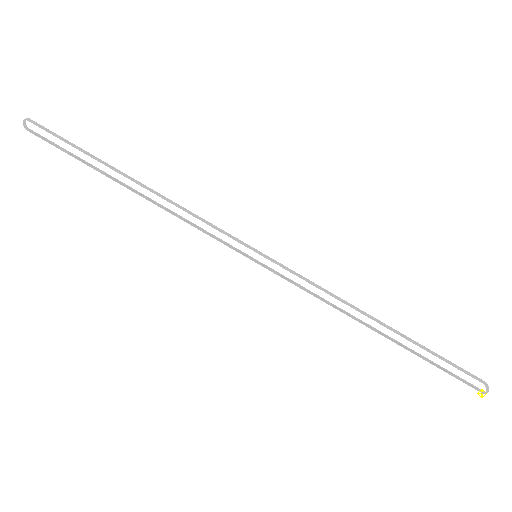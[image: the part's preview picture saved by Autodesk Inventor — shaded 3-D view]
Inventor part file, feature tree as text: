
AUTODESK INVENTOR PART (.ipt)
format: ipt  version: 2025.1 (Build 291241000, 241)  size: 7,425,536 bytes
history: native  units: mm
features: other x361, sketch x3, pattern_linear x2, extrude x2
ambient origin geometry x8: Origin, YZ Plane, XZ Plane, XY Plane, X Axis, Y Axis, Z Axis, Center Point
bodies: Body1 (feature_tree)
feature tree (368):
  other  "Bryła1"
  sketch  "Szkic1"
  other  "Punkt konstrukcyjny1"
  pattern_linear  "Szyk prostokątny1"  Spacing1=27.95mm  [1 undecoded]
  extrude  "Wyciągnięcie proste1"  Depth=1439.872mm
  pattern_linear  "Szyk prostokątny2"  Count1=360 Spacing1=10.0mm
  extrude  "Wyciągnięcie proste2"  Depth=1.0mm
  other  "Punkt konstrukcyjny2"
  other  "Punkt konstrukcyjny3"
  other  "Punkt konstrukcyjny4"
  other  "Punkt konstrukcyjny5"
  other  "Punkt konstrukcyjny6"
  other  "Punkt konstrukcyjny7"
  other  "Punkt konstrukcyjny8"
  other  "Punkt konstrukcyjny9"
  other  "Punkt konstrukcyjny10"
  other  "Punkt konstrukcyjny11"
  other  "Punkt konstrukcyjny12"
  other  "Punkt konstrukcyjny13"
  other  "Punkt konstrukcyjny14"
  other  "Punkt konstrukcyjny15"
  other  "Punkt konstrukcyjny16"
  other  "Punkt konstrukcyjny17"
  other  "Punkt konstrukcyjny18"
  other  "Punkt konstrukcyjny19"
  other  "Punkt konstrukcyjny20"
  other  "Punkt konstrukcyjny21"
  other  "Punkt konstrukcyjny22"
  other  "Punkt konstrukcyjny23"
  other  "Punkt konstrukcyjny24"
  other  "Punkt konstrukcyjny25"
  other  "Punkt konstrukcyjny26"
  other  "Punkt konstrukcyjny27"
  other  "Punkt konstrukcyjny28"
  other  "Punkt konstrukcyjny29"
  other  "Punkt konstrukcyjny30"
  other  "Punkt konstrukcyjny31"
  other  "Punkt konstrukcyjny32"
  other  "Punkt konstrukcyjny33"
  other  "Punkt konstrukcyjny34"
  other  "Punkt konstrukcyjny35"
  other  "Punkt konstrukcyjny36"
  other  "Punkt konstrukcyjny37"
  other  "Punkt konstrukcyjny38"
  other  "Punkt konstrukcyjny39"
  other  "Punkt konstrukcyjny40"
  other  "Punkt konstrukcyjny41"
  other  "Punkt konstrukcyjny42"
  other  "Punkt konstrukcyjny43"
  other  "Punkt konstrukcyjny44"
  other  "Punkt konstrukcyjny45"
  other  "Punkt konstrukcyjny46"
  other  "Punkt konstrukcyjny47"
  other  "Punkt konstrukcyjny48"
  other  "Punkt konstrukcyjny49"
  other  "Punkt konstrukcyjny50"
  other  "Punkt konstrukcyjny51"
  other  "Punkt konstrukcyjny52"
  other  "Punkt konstrukcyjny53"
  other  "Punkt konstrukcyjny54"
  other  "Punkt konstrukcyjny55"
  other  "Punkt konstrukcyjny56"
  other  "Punkt konstrukcyjny57"
  other  "Punkt konstrukcyjny58"
  other  "Punkt konstrukcyjny59"
  other  "Punkt konstrukcyjny60"
  other  "Punkt konstrukcyjny61"
  other  "Punkt konstrukcyjny62"
  other  "Punkt konstrukcyjny63"
  other  "Punkt konstrukcyjny64"
  other  "Punkt konstrukcyjny65"
  other  "Punkt konstrukcyjny66"
  other  "Punkt konstrukcyjny67"
  other  "Punkt konstrukcyjny68"
  other  "Punkt konstrukcyjny69"
  other  "Punkt konstrukcyjny70"
  other  "Punkt konstrukcyjny71"
  other  "Punkt konstrukcyjny72"
  other  "Punkt konstrukcyjny73"
  other  "Punkt konstrukcyjny74"
  other  "Punkt konstrukcyjny75"
  other  "Punkt konstrukcyjny76"
  other  "Punkt konstrukcyjny77"
  other  "Punkt konstrukcyjny78"
  other  "Punkt konstrukcyjny79"
  other  "Punkt konstrukcyjny80"
  other  "Punkt konstrukcyjny81"
  other  "Punkt konstrukcyjny82"
  other  "Punkt konstrukcyjny83"
  other  "Punkt konstrukcyjny84"
  other  "Punkt konstrukcyjny85"
  other  "Punkt konstrukcyjny86"
  other  "Punkt konstrukcyjny87"
  other  "Punkt konstrukcyjny88"
  other  "Punkt konstrukcyjny89"
  other  "Punkt konstrukcyjny90"
  other  "Punkt konstrukcyjny91"
  other  "Punkt konstrukcyjny92"
  other  "Punkt konstrukcyjny93"
  other  "Punkt konstrukcyjny94"
  other  "Punkt konstrukcyjny95"
  other  "Punkt konstrukcyjny96"
  other  "Punkt konstrukcyjny97"
  other  "Punkt konstrukcyjny98"
  other  "Punkt konstrukcyjny99"
  other  "Punkt konstrukcyjny100"
  other  "Punkt konstrukcyjny101"
  other  "Punkt konstrukcyjny102"
  other  "Punkt konstrukcyjny103"
  other  "Punkt konstrukcyjny104"
  other  "Punkt konstrukcyjny105"
  other  "Punkt konstrukcyjny106"
  other  "Punkt konstrukcyjny107"
  other  "Punkt konstrukcyjny108"
  other  "Punkt konstrukcyjny109"
  other  "Punkt konstrukcyjny110"
  other  "Punkt konstrukcyjny111"
  other  "Punkt konstrukcyjny112"
  other  "Punkt konstrukcyjny113"
  other  "Punkt konstrukcyjny114"
  other  "Punkt konstrukcyjny115"
  other  "Punkt konstrukcyjny116"
  other  "Punkt konstrukcyjny117"
  other  "Punkt konstrukcyjny118"
  other  "Punkt konstrukcyjny119"
  other  "Punkt konstrukcyjny120"
  other  "Punkt konstrukcyjny121"
  other  "Punkt konstrukcyjny122"
  other  "Punkt konstrukcyjny123"
  other  "Punkt konstrukcyjny124"
  other  "Punkt konstrukcyjny125"
  other  "Punkt konstrukcyjny126"
  other  "Punkt konstrukcyjny127"
  other  "Punkt konstrukcyjny128"
  other  "Punkt konstrukcyjny129"
  other  "Punkt konstrukcyjny130"
  other  "Punkt konstrukcyjny131"
  other  "Punkt konstrukcyjny132"
  other  "Punkt konstrukcyjny133"
  other  "Punkt konstrukcyjny134"
  other  "Punkt konstrukcyjny135"
  other  "Punkt konstrukcyjny136"
  other  "Punkt konstrukcyjny137"
  other  "Punkt konstrukcyjny138"
  other  "Punkt konstrukcyjny139"
  other  "Punkt konstrukcyjny140"
  other  "Punkt konstrukcyjny141"
  other  "Punkt konstrukcyjny142"
  other  "Punkt konstrukcyjny143"
  other  "Punkt konstrukcyjny144"
  other  "Punkt konstrukcyjny145"
  other  "Punkt konstrukcyjny146"
  other  "Punkt konstrukcyjny147"
  other  "Punkt konstrukcyjny148"
  other  "Punkt konstrukcyjny149"
  other  "Punkt konstrukcyjny150"
  other  "Punkt konstrukcyjny151"
  other  "Punkt konstrukcyjny152"
  other  "Punkt konstrukcyjny153"
  other  "Punkt konstrukcyjny154"
  other  "Punkt konstrukcyjny155"
  other  "Punkt konstrukcyjny156"
  other  "Punkt konstrukcyjny157"
  other  "Punkt konstrukcyjny158"
  other  "Punkt konstrukcyjny159"
  other  "Punkt konstrukcyjny160"
  other  "Punkt konstrukcyjny161"
  other  "Punkt konstrukcyjny162"
  other  "Punkt konstrukcyjny163"
  other  "Punkt konstrukcyjny164"
  other  "Punkt konstrukcyjny165"
  other  "Punkt konstrukcyjny166"
  other  "Punkt konstrukcyjny167"
  other  "Punkt konstrukcyjny168"
  other  "Punkt konstrukcyjny169"
  other  "Punkt konstrukcyjny170"
  other  "Punkt konstrukcyjny171"
  other  "Punkt konstrukcyjny172"
  other  "Punkt konstrukcyjny173"
  other  "Punkt konstrukcyjny174"
  other  "Punkt konstrukcyjny175"
  other  "Punkt konstrukcyjny176"
  other  "Punkt konstrukcyjny177"
  other  "Punkt konstrukcyjny178"
  other  "Punkt konstrukcyjny179"
  other  "Punkt konstrukcyjny180"
  other  "Punkt konstrukcyjny181"
  other  "Punkt konstrukcyjny182"
  other  "Punkt konstrukcyjny183"
  other  "Punkt konstrukcyjny184"
  other  "Punkt konstrukcyjny185"
  other  "Punkt konstrukcyjny186"
  other  "Punkt konstrukcyjny187"
  other  "Punkt konstrukcyjny188"
  other  "Punkt konstrukcyjny189"
  other  "Punkt konstrukcyjny190"
  other  "Punkt konstrukcyjny191"
  other  "Punkt konstrukcyjny192"
  other  "Punkt konstrukcyjny193"
  other  "Punkt konstrukcyjny194"
  other  "Punkt konstrukcyjny195"
  other  "Punkt konstrukcyjny196"
  other  "Punkt konstrukcyjny197"
  other  "Punkt konstrukcyjny198"
  other  "Punkt konstrukcyjny199"
  other  "Punkt konstrukcyjny200"
  other  "Punkt konstrukcyjny201"
  other  "Punkt konstrukcyjny202"
  other  "Punkt konstrukcyjny203"
  other  "Punkt konstrukcyjny204"
  other  "Punkt konstrukcyjny205"
  other  "Punkt konstrukcyjny206"
  other  "Punkt konstrukcyjny207"
  other  "Punkt konstrukcyjny208"
  other  "Punkt konstrukcyjny209"
  other  "Punkt konstrukcyjny210"
  other  "Punkt konstrukcyjny211"
  other  "Punkt konstrukcyjny212"
  other  "Punkt konstrukcyjny213"
  other  "Punkt konstrukcyjny214"
  other  "Punkt konstrukcyjny215"
  other  "Punkt konstrukcyjny216"
  other  "Punkt konstrukcyjny217"
  other  "Punkt konstrukcyjny218"
  other  "Punkt konstrukcyjny219"
  other  "Punkt konstrukcyjny220"
  other  "Punkt konstrukcyjny221"
  other  "Punkt konstrukcyjny222"
  other  "Punkt konstrukcyjny223"
  other  "Punkt konstrukcyjny224"
  other  "Punkt konstrukcyjny225"
  other  "Punkt konstrukcyjny226"
  other  "Punkt konstrukcyjny227"
  other  "Punkt konstrukcyjny228"
  other  "Punkt konstrukcyjny229"
  other  "Punkt konstrukcyjny230"
  other  "Punkt konstrukcyjny231"
  other  "Punkt konstrukcyjny232"
  other  "Punkt konstrukcyjny233"
  other  "Punkt konstrukcyjny234"
  other  "Punkt konstrukcyjny235"
  other  "Punkt konstrukcyjny236"
  other  "Punkt konstrukcyjny237"
  other  "Punkt konstrukcyjny238"
  other  "Punkt konstrukcyjny239"
  other  "Punkt konstrukcyjny240"
  other  "Punkt konstrukcyjny241"
  other  "Punkt konstrukcyjny242"
  other  "Punkt konstrukcyjny243"
  other  "Punkt konstrukcyjny244"
  other  "Punkt konstrukcyjny245"
  other  "Punkt konstrukcyjny246"
  other  "Punkt konstrukcyjny247"
  other  "Punkt konstrukcyjny248"
  other  "Punkt konstrukcyjny249"
  other  "Punkt konstrukcyjny250"
  other  "Punkt konstrukcyjny251"
  other  "Punkt konstrukcyjny252"
  other  "Punkt konstrukcyjny253"
  other  "Punkt konstrukcyjny254"
  other  "Punkt konstrukcyjny255"
  other  "Punkt konstrukcyjny256"
  other  "Punkt konstrukcyjny257"
  other  "Punkt konstrukcyjny258"
  other  "Punkt konstrukcyjny259"
  other  "Punkt konstrukcyjny260"
  other  "Punkt konstrukcyjny261"
  other  "Punkt konstrukcyjny262"
  other  "Punkt konstrukcyjny263"
  other  "Punkt konstrukcyjny264"
  other  "Punkt konstrukcyjny265"
  other  "Punkt konstrukcyjny266"
  other  "Punkt konstrukcyjny267"
  other  "Punkt konstrukcyjny268"
  other  "Punkt konstrukcyjny269"
  other  "Punkt konstrukcyjny270"
  other  "Punkt konstrukcyjny271"
  other  "Punkt konstrukcyjny272"
  other  "Punkt konstrukcyjny273"
  other  "Punkt konstrukcyjny274"
  other  "Punkt konstrukcyjny275"
  other  "Punkt konstrukcyjny276"
  other  "Punkt konstrukcyjny277"
  other  "Punkt konstrukcyjny278"
  other  "Punkt konstrukcyjny279"
  other  "Punkt konstrukcyjny280"
  other  "Punkt konstrukcyjny281"
  other  "Punkt konstrukcyjny282"
  other  "Punkt konstrukcyjny283"
  other  "Punkt konstrukcyjny284"
  other  "Punkt konstrukcyjny285"
  other  "Punkt konstrukcyjny286"
  other  "Punkt konstrukcyjny287"
  other  "Punkt konstrukcyjny288"
  other  "Punkt konstrukcyjny289"
  other  "Punkt konstrukcyjny290"
  other  "Punkt konstrukcyjny291"
  other  "Punkt konstrukcyjny292"
  other  "Punkt konstrukcyjny293"
  other  "Punkt konstrukcyjny294"
  other  "Punkt konstrukcyjny295"
  other  "Punkt konstrukcyjny296"
  other  "Punkt konstrukcyjny297"
  other  "Punkt konstrukcyjny298"
  other  "Punkt konstrukcyjny299"
  other  "Punkt konstrukcyjny300"
  other  "Punkt konstrukcyjny301"
  other  "Punkt konstrukcyjny302"
  other  "Punkt konstrukcyjny303"
  other  "Punkt konstrukcyjny304"
  other  "Punkt konstrukcyjny305"
  other  "Punkt konstrukcyjny306"
  other  "Punkt konstrukcyjny307"
  other  "Punkt konstrukcyjny308"
  other  "Punkt konstrukcyjny309"
  other  "Punkt konstrukcyjny310"
  other  "Punkt konstrukcyjny311"
  other  "Punkt konstrukcyjny312"
  other  "Punkt konstrukcyjny313"
  other  "Punkt konstrukcyjny314"
  other  "Punkt konstrukcyjny315"
  other  "Punkt konstrukcyjny316"
  other  "Punkt konstrukcyjny317"
  other  "Punkt konstrukcyjny318"
  other  "Punkt konstrukcyjny319"
  other  "Punkt konstrukcyjny320"
  other  "Punkt konstrukcyjny321"
  other  "Punkt konstrukcyjny322"
  other  "Punkt konstrukcyjny323"
  other  "Punkt konstrukcyjny324"
  other  "Punkt konstrukcyjny325"
  other  "Punkt konstrukcyjny326"
  other  "Punkt konstrukcyjny327"
  other  "Punkt konstrukcyjny328"
  other  "Punkt konstrukcyjny329"
  other  "Punkt konstrukcyjny330"
  other  "Punkt konstrukcyjny331"
  other  "Punkt konstrukcyjny332"
  other  "Punkt konstrukcyjny333"
  other  "Punkt konstrukcyjny334"
  other  "Punkt konstrukcyjny335"
  other  "Punkt konstrukcyjny336"
  other  "Punkt konstrukcyjny337"
  other  "Punkt konstrukcyjny338"
  other  "Punkt konstrukcyjny339"
  other  "Punkt konstrukcyjny340"
  other  "Punkt konstrukcyjny341"
  other  "Punkt konstrukcyjny342"
  other  "Punkt konstrukcyjny343"
  other  "Punkt konstrukcyjny344"
  other  "Punkt konstrukcyjny345"
  other  "Punkt konstrukcyjny346"
  other  "Punkt konstrukcyjny347"
  other  "Punkt konstrukcyjny348"
  other  "Punkt konstrukcyjny349"
  other  "Punkt konstrukcyjny350"
  other  "Punkt konstrukcyjny351"
  other  "Punkt konstrukcyjny352"
  other  "Punkt konstrukcyjny353"
  other  "Punkt konstrukcyjny354"
  other  "Punkt konstrukcyjny355"
  other  "Punkt konstrukcyjny356"
  other  "Punkt konstrukcyjny357"
  other  "Punkt konstrukcyjny358"
  other  "Punkt konstrukcyjny359"
  other  "Punkt konstrukcyjny360"
  sketch  "Szkic6"
  sketch  "Szkic7"
note: 1 required parameter value undecoded (feature->parameter linkage not recoverable at this tier; creation-order binding heuristic only, values carry confidence <= 0.55)
